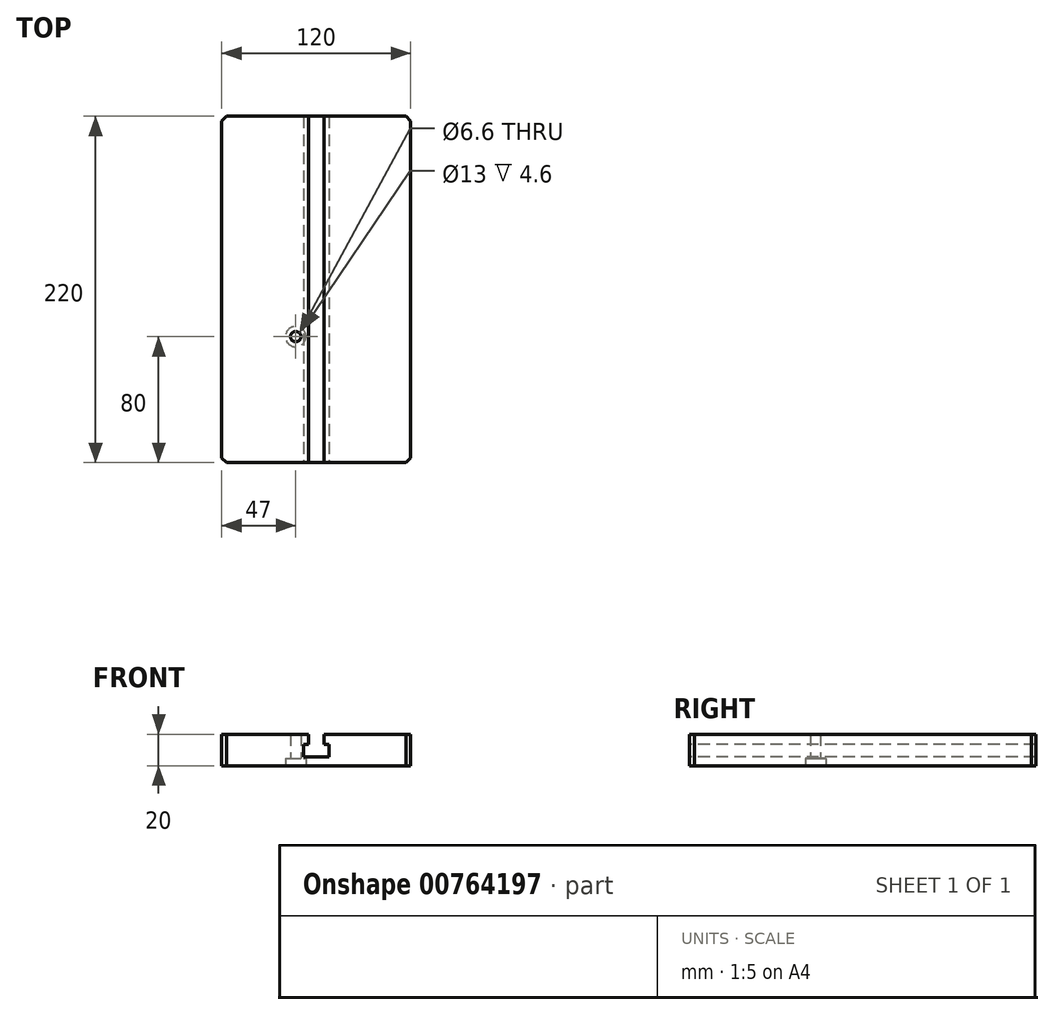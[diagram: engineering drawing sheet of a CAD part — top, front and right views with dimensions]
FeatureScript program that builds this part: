
annotation { "Feature Type Name" : "Feature", "Feature Type Description" : "" }
export const myFeature = defineFeature(function(context is Context, id is Id, definition is map)
    precondition{}
    {
        {
            var Q0;
            Q0=qCreatedBy(makeId("Top.planeOp"),FACE);
            var sketch = newSketch(context, id + "F0", { "sketchPlane" : qUnion([Q0])});
            skLineSegment(sketch, "E0.bottom", {"start": v(-60, 110) * mm, "end": v(60, 110) * mm});
            skLineSegment(sketch, "E0.top", {"start": v(-60, -110) * mm, "end": v(60, -110) * mm});
            skLineSegment(sketch, "E0.left", {"start": v(-60, 110) * mm, "end": v(-60, -110) * mm});
            skLineSegment(sketch, "E0.right", {"start": v(60, 110) * mm, "end": v(60, -110) * mm});
            skPoint(sketch, "E0.middle", {"position": v(0, 0) * mm});
            skSolve(sketch);
        }
        {
            var Q0;
            Q0 = qSketchRegion(id + "F0", true);
            extrude(context, id + "F1", {"entities" : qUnion([Q0]), "endBound" : BoundingType.SYMMETRIC, "depth" : 20 * mm, "offsetDistance" : 25 * mm});
        }
        {
            var Q0;
            Q0=makeQuery(id+"F1.opExtrude","SWEPT_FACE",FACE,{"disambiguationData":[OSD([sQuery(id+"F0.wireOp",EDGE,"E0.top")])]});
            var sketch = newSketch(context, id + "F2", { "sketchPlane" : qUnion([Q0])});
            skLineSegment(sketch, "E1", {"start": v(-5, 10) * mm, "end": v(-5, 3.5) * mm});
            skLineSegment(sketch, "E2", {"start": v(-5, 3.5) * mm, "end": v(-8, 3.5) * mm});
            skLineSegment(sketch, "E3", {"start": v(-8, 3.5) * mm, "end": v(-8, -4.5) * mm});
            skLineSegment(sketch, "E4", {"start": v(-8, -4.5) * mm, "end": v(8, -4.5) * mm});
            skLineSegment(sketch, "E5", {"start": v(8, -4.5) * mm, "end": v(8, 3.5) * mm});
            skLineSegment(sketch, "E6", {"start": v(8, 3.5) * mm, "end": v(5, 3.5) * mm});
            skLineSegment(sketch, "E7", {"start": v(5, 3.5) * mm, "end": v(5, 10) * mm});
            skLineSegment(sketch, "E8", {"start": v(5, 10) * mm, "end": v(-5, 10) * mm});
            skLineSegment(sketch, "E9", {"start": v(0, 10) * mm, "end": v(0, 0) * mm, "construction": true});
            skSolve(sketch);
        }
        {
            var Q0;
            Q0=makeQuery(id+"F2.imprint","IMPRINT",FACE,{"disambiguationData":[TD([[makeQuery(id+"F2.imprint","IMPRINT",EDGE,{"derivedFrom":sQuery(id+"F2.wireOp",EDGE,"E1")}),1.0]])]});
            extrude(context, id + "F3", {"entities" : qUnion([Q0]), "operationType" : NewBodyOperationType.REMOVE, "endBound" : BoundingType.THROUGH_ALL, "oppositeDirection" : true, "depth" : 25 * mm, "offsetDistance" : 25 * mm});
        }
        {
            var Q0;
            Q0=makeQuery(id+"F1.opExtrude","SWEPT_EDGE",EDGE,{"disambiguationData":[OSD([sQuery(id+"F0.wireOp",EDGE,"E0.top"),sQuery(id+"F0.wireOp",EDGE,"E0.right")])]});
            var Q1;
            Q1=makeQuery(id+"F1.opExtrude","SWEPT_EDGE",EDGE,{"disambiguationData":[OSD([sQuery(id+"F0.wireOp",EDGE,"E0.bottom"),sQuery(id+"F0.wireOp",EDGE,"E0.right")])]});
            var Q2;
            Q2=makeQuery(id+"F1.opExtrude","SWEPT_EDGE",EDGE,{"disambiguationData":[OSD([sQuery(id+"F0.wireOp",EDGE,"E0.bottom"),sQuery(id+"F0.wireOp",EDGE,"E0.left")])]});
            var Q3;
            Q3=makeQuery(id+"F1.opExtrude","SWEPT_EDGE",EDGE,{"disambiguationData":[OSD([sQuery(id+"F0.wireOp",EDGE,"E0.top"),sQuery(id+"F0.wireOp",EDGE,"E0.left")])]});
            chamfer(context, id + "F4", {"entities" : qUnion([Q0, Q1, Q2, Q3]), "width" : 3 * mm, "tangentPropagation" : true});
        }
        {
            var Q0;
            Q0=makeQuery(id+"F1.opExtrude","CAP_FACE",FACE,{"disambiguationData":[OSD([sQuery(id+"F0.wireOp",EDGE,"E0.bottom"),sQuery(id+"F0.wireOp",EDGE,"E0.top"),sQuery(id+"F0.wireOp",EDGE,"E0.left"),sQuery(id+"F0.wireOp",EDGE,"E0.right")])],"isStart":true});
            var sketch = newSketch(context, id + "F5", { "sketchPlane" : qUnion([Q0])});
            skPoint(sketch, "E10", {"position": v(-13, 30) * mm});
            skSolve(sketch);
        }
        {
            var Q0;
            Q0=sQuery(id+"F5.wireOp",VERTEX,"E10");
            var Q1;
            Q1=makeQuery(id+"F1.opExtrude","SWEPT_BODY",BODY,{"disambiguationData":[OSD([sQuery(id+"F0.wireOp",EDGE,"E0.bottom"),sQuery(id+"F0.wireOp",EDGE,"E0.top"),sQuery(id+"F0.wireOp",EDGE,"E0.left"),sQuery(id+"F0.wireOp",EDGE,"E0.right")])]});
            hole(context, id + "F6", {"style" : HoleStyle.C_BORE, "endStyle" : HoleEndStyle.THROUGH, "holeDiameter" : 6.6 * mm, "cBoreDiameter" : 13 * mm, "cBoreDepth" : 4.6 * mm, "majorDiameter" : 5 * mm, "isTappedThrough" : true, "tappedDepth" : 12 * mm, "tapClearance" : 3, "locations" : qUnion([Q0]), "scope" : qUnion([Q1])});
        }
    });
